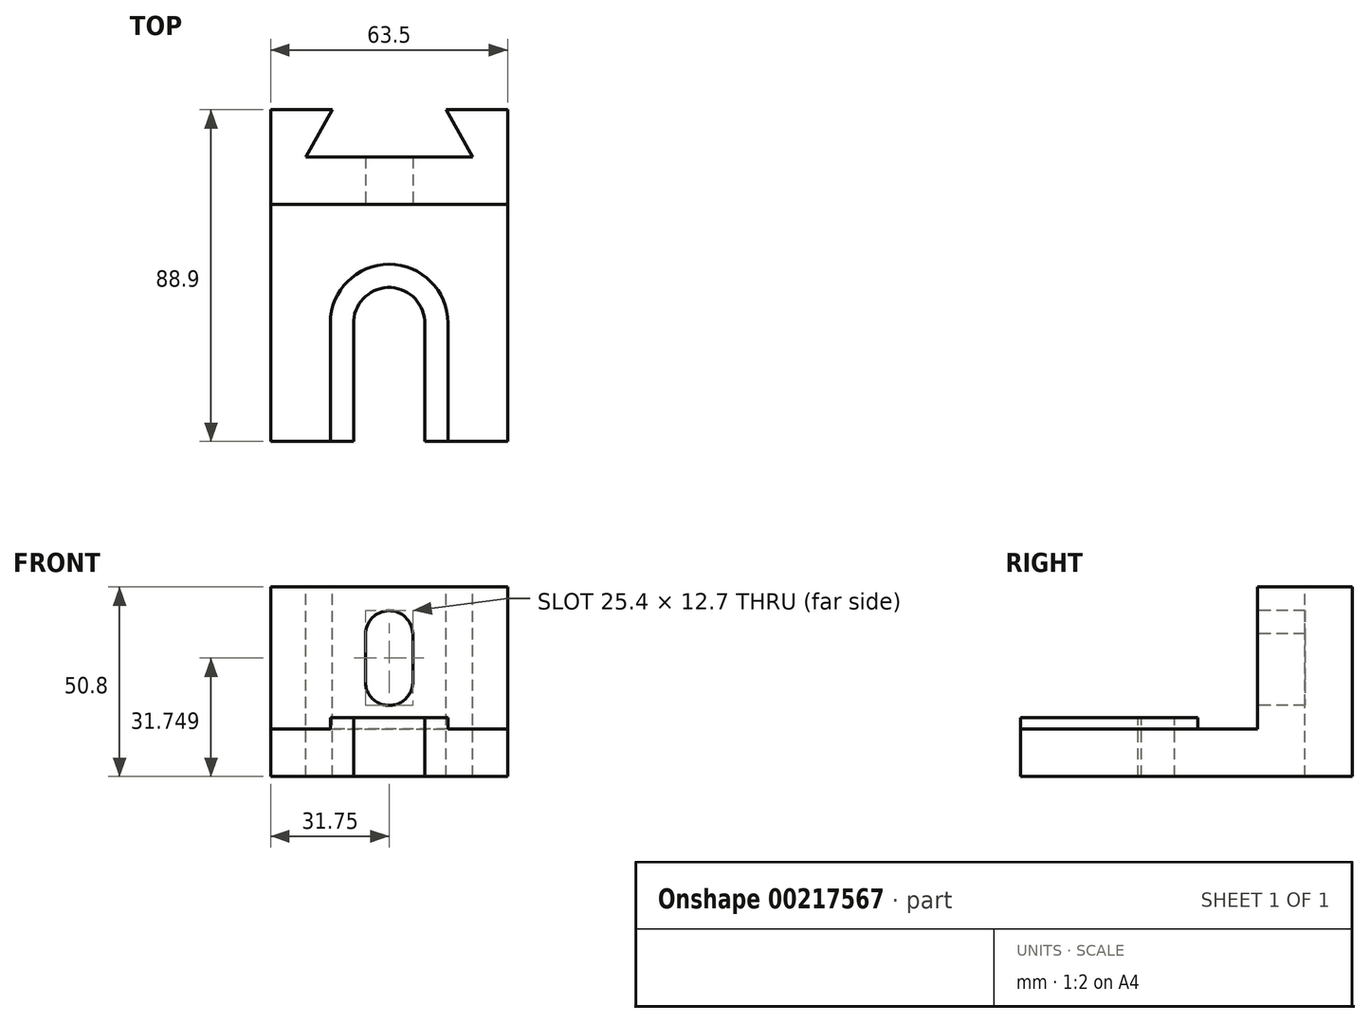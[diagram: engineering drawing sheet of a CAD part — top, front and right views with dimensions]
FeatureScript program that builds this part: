
annotation { "Feature Type Name" : "Feature", "Feature Type Description" : "" }
export const myFeature = defineFeature(function(context is Context, id is Id, definition is map)
    precondition{}
    {
        {
            var Q0;
            Q0=qCreatedBy(makeId("Front.planeOp"),FACE);
            var sketch = newSketch(context, id + "F0", { "sketchPlane" : qUnion([Q0])});
            skLineSegment(sketch, "E0.bottom", {"start": v(31.75, -25.4) * mm, "end": v(-31.75, -25.4) * mm});
            skLineSegment(sketch, "E0.top", {"start": v(31.75, 25.4) * mm, "end": v(-31.75, 25.4) * mm});
            skLineSegment(sketch, "E0.left", {"start": v(31.75, -25.4) * mm, "end": v(31.75, 25.4) * mm});
            skLineSegment(sketch, "E0.right", {"start": v(-31.75, -25.4) * mm, "end": v(-31.75, 25.4) * mm});
            skPoint(sketch, "E0.middle", {"position": v(0, 0) * mm});
            skSolve(sketch);
        }
        {
            var Q0;
            Q0=makeQuery(id+"F0.imprint","IMPRINT",FACE,{"disambiguationData":[TD([[makeQuery(id+"F0.imprint","IMPRINT",EDGE,{"derivedFrom":sQuery(id+"F0.wireOp",EDGE,"E0.bottom")}),-1.0]])]});
            extrude(context, id + "F1", {"entities" : qUnion([Q0]), "depth" : 88.9 * mm});
        }
        {
            var Q0;
            Q0=makeQuery(id+"F1.opExtrude","SWEPT_FACE",FACE,{"disambiguationData":[OSD([sQuery(id+"F0.wireOp",EDGE,"E0.left")])]});
            var sketch = newSketch(context, id + "F2", { "sketchPlane" : qUnion([Q0])});
            skLineSegment(sketch, "E1", {"start": v(0, -25.4) * mm, "end": v(-25.4, -25.4) * mm});
            skLineSegment(sketch, "E2", {"start": v(-25.4, -12.7) * mm, "end": v(-25.4, 25.4) * mm});
            skLineSegment(sketch, "E3", {"start": v(-25.4, 25.4) * mm, "end": v(0, 25.4) * mm});
            skLineSegment(sketch, "E4", {"start": v(-88.9, -25.4) * mm, "end": v(-88.9, -12.7) * mm});
            skLineSegment(sketch, "E5", {"start": v(-88.9, -12.7) * mm, "end": v(-25.4, -12.7) * mm});
            skSolve(sketch);
        }
        {
            var Q0;
            {var subQ0=sQuery(id+"F2.wireOp",EDGE,"E2");Q0=makeQuery(id+"F2.imprint","IMPRINT",FACE,{"disambiguationData":[TD([[makeQuery(id+"F2.imprint","IMPRINT",EDGE,{"derivedFrom":subQ0}),1.0]])]});}
            extrude(context, id + "F3", {"entities" : qUnion([Q0]), "operationType" : NewBodyOperationType.REMOVE, "endBound" : BoundingType.THROUGH_ALL, "oppositeDirection" : true, "depth" : 25.4 * mm});
        }
        {
            var Q0;
            Q0=makeQuery(id+"F3.boolean.opBoolean","COPY",FACE,{"derivedFrom":makeQuery(id+"F3.opExtrude","SWEPT_FACE",FACE,{"disambiguationData":[OSD([sQuery(id+"F2.wireOp",EDGE,"E5")])]})});
            var sketch = newSketch(context, id + "F4", { "sketchPlane" : qUnion([Q0])});
            skLineSegment(sketch, "E6", {"start": v(31.75, -88.9) * mm, "end": v(0, -88.9) * mm});
            skArc(sketch, "E7", {"start": v(9.52, -57.44) * mm, "mid": v(0.48, -47.64) * mm, "end": v(-9.5, -56.48) * mm});
            skLineSegment(sketch, "E8", {"start": v(-9.5, -56.48) * mm, "end": v(-9.5, -88.9) * mm});
            skLineSegment(sketch, "E9", {"start": v(9.52, -57.44) * mm, "end": v(9.52, -88.9) * mm});
            skLineSegment(sketch, "E10", {"start": v(-9.5, -88.9) * mm, "end": v(9.52, -88.9) * mm});
            skSolve(sketch);
        }
        {
            var Q0;
            Q0=makeQuery(id+"F4.imprint","IMPRINT",FACE,{"disambiguationData":[TD([[makeQuery(id+"F4.imprint","IMPRINT",EDGE,{"derivedFrom":sQuery(id+"F4.wireOp",EDGE,"E7")}),1.0]])]});
            extrude(context, id + "F5", {"entities" : qUnion([Q0]), "operationType" : NewBodyOperationType.REMOVE, "endBound" : BoundingType.THROUGH_ALL, "oppositeDirection" : true, "depth" : 25.4 * mm});
        }
        {
            var Q0;
            Q0=makeQuery(id+"F3.boolean.opBoolean","COPY",FACE,{"derivedFrom":makeQuery(id+"F3.opExtrude","SWEPT_FACE",FACE,{"disambiguationData":[OSD([sQuery(id+"F2.wireOp",EDGE,"E5")])]})});
            var sketch = newSketch(context, id + "F6", { "sketchPlane" : qUnion([Q0])});
            skArc(sketch, "E11", {"start": v(15.75, -57.15) * mm, "mid": v(0, -41.4) * mm, "end": v(-15.75, -57.15) * mm});
            skLineSegment(sketch, "E12", {"start": v(-15.75, -57.15) * mm, "end": v(-15.75, -88.9) * mm});
            skLineSegment(sketch, "E13", {"start": v(15.75, -57.15) * mm, "end": v(15.75, -88.9) * mm});
            skSolve(sketch);
        }
        {
            var Q0;
            Q0=makeQuery(id+"F6.imprint","IMPRINT",FACE,{"disambiguationData":[TD([[makeQuery(id+"F6.imprint","IMPRINT",EDGE,{"derivedFrom":sQuery(id+"F6.wireOp",EDGE,"E11")}),1.0]])]});
            extrude(context, id + "F7", {"entities" : qUnion([Q0]), "operationType" : NewBodyOperationType.ADD, "depth" : 3.05 * mm});
        }
        {
            var Q0;
            Q0=makeQuery(id+"F3.boolean.opBoolean","COPY",FACE,{"derivedFrom":makeQuery(id+"F3.opExtrude","SWEPT_FACE",FACE,{"disambiguationData":[OSD([sQuery(id+"F2.wireOp",EDGE,"E2")])]})});
            var sketch = newSketch(context, id + "F8", { "sketchPlane" : qUnion([Q0])});
            skLineSegment(sketch, "E14", {"start": v(0, 25.4) * mm, "end": v(0, 12.7) * mm});
            skPoint(sketch, "E14.endSnap0", {"position": v(0, 25.4) * mm});
            skArc(sketch, "E15", {"start": v(6.35, 12.93) * mm, "mid": v(-0.11, 19.05) * mm, "end": v(-6.35, 12.7) * mm});
            skLineSegment(sketch, "E16", {"start": v(0, 12.7) * mm, "end": v(0, 0) * mm});
            skArc(sketch, "E17", {"start": v(-6.35, 0) * mm, "mid": v(0, -6.35) * mm, "end": v(6.35, 0) * mm});
            skLineSegment(sketch, "E18", {"start": v(0, 12.7) * mm, "end": v(-6.35, 12.7) * mm});
            skLineSegment(sketch, "E19", {"start": v(-6.35, 12.7) * mm, "end": v(-6.35, 0) * mm});
            skLineSegment(sketch, "E20", {"start": v(6.35, 12.93) * mm, "end": v(6.35, 0) * mm});
            skSolve(sketch);
        }
        {
            var Q0;
            {var subQ1=sQuery(id+"F8.wireOp",EDGE,"E17");Q0=makeQuery(id+"F8.imprint","IMPRINT",FACE,{"disambiguationData":[TD([[makeQuery(id+"F8.imprint","IMPRINT",EDGE,{"derivedFrom":subQ1}),1.0]])]});}
            var Q1;
            {var subQ0=sQuery(id+"F8.wireOp",EDGE,"E18");Q1=makeQuery(id+"F8.imprint","IMPRINT",FACE,{"disambiguationData":[TD([[makeQuery(id+"F8.imprint","IMPRINT",EDGE,{"derivedFrom":subQ0}),-1.0]])]});}
            extrude(context, id + "F9", {"entities" : qUnion([Q0, Q1]), "operationType" : NewBodyOperationType.REMOVE, "endBound" : BoundingType.THROUGH_ALL, "oppositeDirection" : true, "depth" : 25.4 * mm});
        }
        {
            var Q0;
            Q0=makeQuery(id+"F1.opExtrude","SWEPT_FACE",FACE,{"disambiguationData":[OSD([sQuery(id+"F0.wireOp",EDGE,"E0.top")])]});
            var sketch = newSketch(context, id + "F10", { "sketchPlane" : qUnion([Q0])});
            skLineSegment(sketch, "E21", {"start": v(0, 0) * mm, "end": v(0, -12.7) * mm});
            skLineSegment(sketch, "E22", {"start": v(0, -12.7) * mm, "end": v(-22.35, -12.7) * mm});
            skLineSegment(sketch, "E23", {"start": v(0, -12.7) * mm, "end": v(22.35, -12.7) * mm});
            skLineSegment(sketch, "E24", {"start": v(0, 0) * mm, "end": v(15.24, 0) * mm});
            skLineSegment(sketch, "E25", {"start": v(0, 0) * mm, "end": v(-15.24, 0) * mm});
            skLineSegment(sketch, "E26", {"start": v(-22.35, -12.7) * mm, "end": v(-15.24, 0) * mm});
            skLineSegment(sketch, "E27", {"start": v(22.35, -12.7) * mm, "end": v(15.24, 0) * mm});
            skSolve(sketch);
        }
        {
            var Q0;
            Q0=makeQuery(id+"F10.imprint","IMPRINT",FACE,{"disambiguationData":[TD([[makeQuery(id+"F10.imprint","IMPRINT",EDGE,{"derivedFrom":sQuery(id+"F10.wireOp",EDGE,"E21")}),-1.0]])]});
            var Q1;
            Q1=makeQuery(id+"F10.imprint","IMPRINT",FACE,{"disambiguationData":[TD([[makeQuery(id+"F10.imprint","IMPRINT",EDGE,{"derivedFrom":sQuery(id+"F10.wireOp",EDGE,"E21")}),1.0]])]});
            extrude(context, id + "F11", {"entities" : qUnion([Q0, Q1]), "operationType" : NewBodyOperationType.REMOVE, "endBound" : BoundingType.THROUGH_ALL, "oppositeDirection" : true, "depth" : 25.4 * mm});
        }
    });
